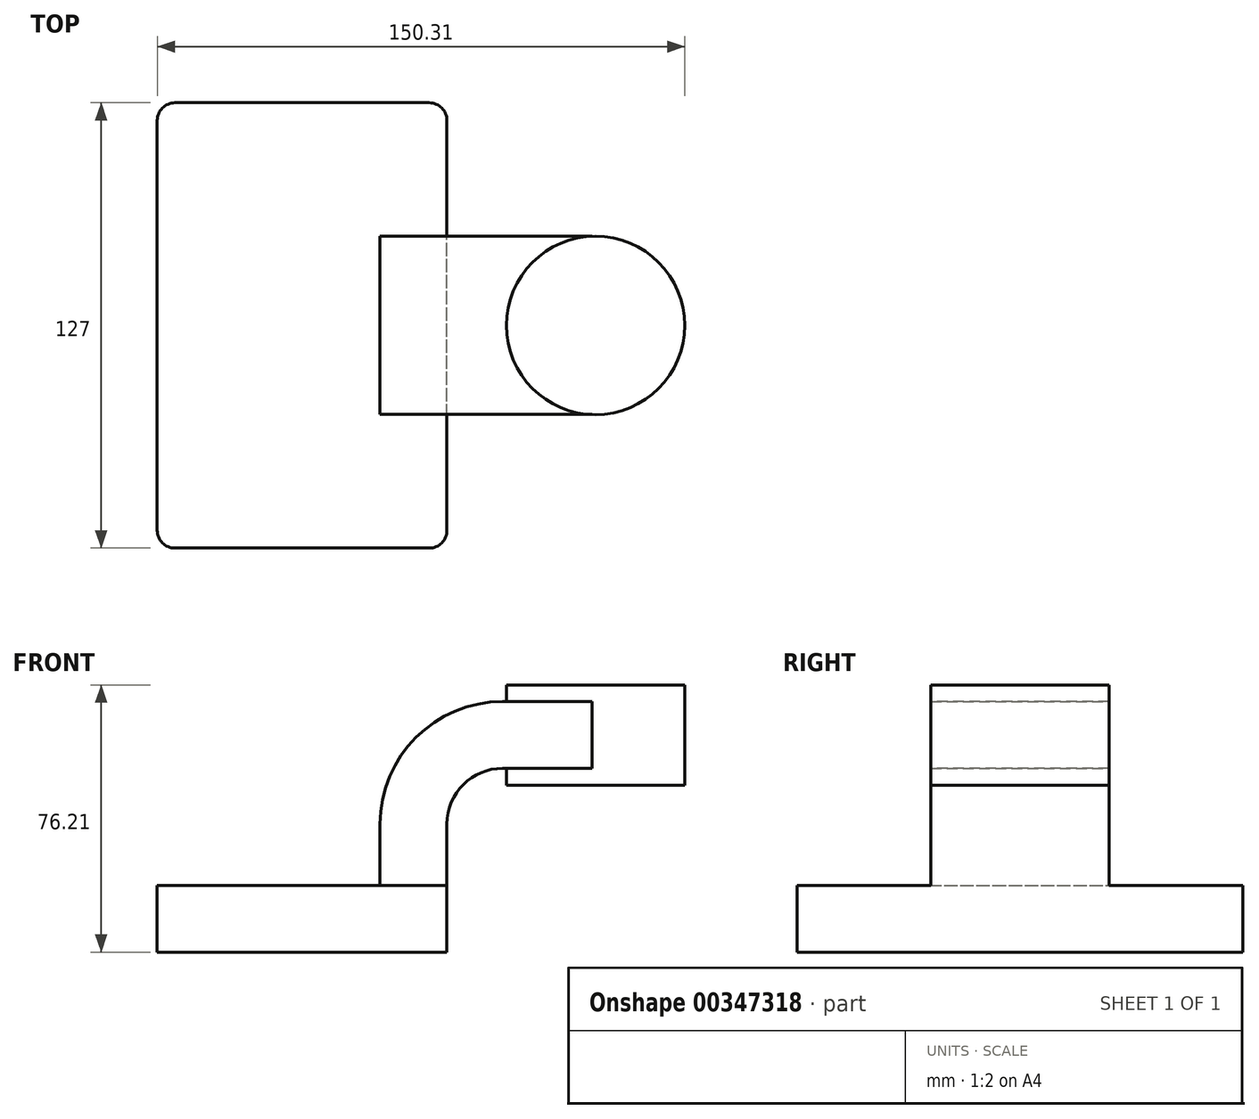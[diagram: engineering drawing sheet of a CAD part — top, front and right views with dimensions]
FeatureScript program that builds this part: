
annotation { "Feature Type Name" : "Feature", "Feature Type Description" : "" }
export const myFeature = defineFeature(function(context is Context, id is Id, definition is map)
    precondition{}
    {
        {
            var Q0;
            Q0=qCreatedBy(makeId("Front.planeOp"),FACE);
            var sketch = newSketch(context, id + "F0", { "sketchPlane" : qUnion([Q0])});
            skLineSegment(sketch, "E0.bottom", {"start": v(41.28, 9.53) * mm, "end": v(-41.28, 9.53) * mm});
            skLineSegment(sketch, "E0.top", {"start": v(41.28, -9.53) * mm, "end": v(-41.28, -9.53) * mm});
            skLineSegment(sketch, "E0.left", {"start": v(41.28, 9.53) * mm, "end": v(41.28, -9.53) * mm});
            skLineSegment(sketch, "E0.right", {"start": v(-41.28, 9.53) * mm, "end": v(-41.28, -9.53) * mm});
            skPoint(sketch, "E0.middle", {"position": v(0, 0) * mm});
            skLineSegment(sketch, "E1.bottom", {"start": v(109.04, 38.1) * mm, "end": v(58.24, 38.1) * mm});
            skLineSegment(sketch, "E1.top", {"start": v(109.04, 66.68) * mm, "end": v(58.24, 66.68) * mm});
            skLineSegment(sketch, "E1.left", {"start": v(109.04, 38.1) * mm, "end": v(109.04, 66.68) * mm});
            skLineSegment(sketch, "E1.right", {"start": v(58.24, 38.1) * mm, "end": v(58.24, 66.68) * mm});
            skPoint(sketch, "E1.middle", {"position": v(83.64, 52.39) * mm});
            skLineSegment(sketch, "E2", {"start": v(41.28, 9.53) * mm, "end": v(41.28, 27) * mm});
            skArc(sketch, "E3", {"start": v(41.27, 27) * mm, "mid": v(45.92, 38.23) * mm, "end": v(57.15, 42.88) * mm});
            skLineSegment(sketch, "E4", {"start": v(57.15, 42.88) * mm, "end": v(83.64, 42.88) * mm});
            skArc(sketch, "E5.0", {"start": v(22.22, 27) * mm, "mid": v(32.45, 51.7) * mm, "end": v(57.15, 61.93) * mm});
            skLineSegment(sketch, "E6.0", {"start": v(22.22, 9.53) * mm, "end": v(22.22, 27) * mm});
            skLineSegment(sketch, "E7.0", {"start": v(57.15, 61.93) * mm, "end": v(83.62, 61.93) * mm});
            skLineSegment(sketch, "E8", {"start": v(83.62, 66.68) * mm, "end": v(83.62, 38.1) * mm});
            skPoint(sketch, "E8.startSnap0", {"position": v(83.64, 66.68) * mm});
            skFitSpline(sketch, "E9", {"points": [v(-41.28, 9.53) * mm, v(57.15, 61.93) * mm], "startDerivative": vector(49, 106.39) * mm, "endDerivative": vector(66.54, -7.38) * mm});
            skSolve(sketch);
        }
        {
            var Q0;
            Q0=makeQuery(id+"F0.imprint","IMPRINT",FACE,{"disambiguationData":[TD([[makeQuery(id+"F0.imprint","IMPRINT",EDGE,{"derivedFrom":sQuery(id+"F0.wireOp",EDGE,"E0.top")}),-1.0]])]});
            extrude(context, id + "F1", {"entities" : qUnion([Q0]), "endBound" : BoundingType.SYMMETRIC, "depth" : 127 * mm});
        }
        {
            var Q0;
            {var subQ0=sQuery(id+"F0.wireOp",EDGE,"E4");var subQ1=sQuery(id+"F0.wireOp",EDGE,"E1.right");var subQ2=makeQuery(id+"F0.imprint","INTERSECT",VERTEX,{"derivedFrom":[subQ1,subQ0]});Q0=makeQuery(id+"F0.imprint","IMPRINT",FACE,{"disambiguationData":[TD([[makeQuery(id+"F0.imprint","IMPRINT",EDGE,{"disambiguationData":[TD([[subQ2,-1.0]])],"derivedFrom":subQ1}),-1.0]])]});}
            var Q1;
            {var subQ1=sQuery(id+"F0.wireOp",EDGE,"E2");Q1=makeQuery(id+"F0.imprint","IMPRINT",FACE,{"disambiguationData":[TD([[makeQuery(id+"F0.imprint","IMPRINT",EDGE,{"derivedFrom":subQ1}),1.0]])]});}
            extrude(context, id + "F2", {"entities" : qUnion([Q0, Q1]), "operationType" : NewBodyOperationType.ADD, "endBound" : BoundingType.SYMMETRIC, "depth" : 50.8 * mm});
        }
        {
            var Q0;
            Q0=makeQuery(id+"F0.imprint","IMPRINT",FACE,{"disambiguationData":[TD([[makeQuery(id+"F0.imprint","IMPRINT",EDGE,{"derivedFrom":sQuery(id+"F0.wireOp",EDGE,"E5.0")}),1.0]])]});
            extrude(context, id + "F3", {"entities" : qUnion([Q0]), "operationType" : NewBodyOperationType.ADD, "endBound" : BoundingType.SYMMETRIC, "depth" : 15.88 * mm});
        }
        {
            var Q0;
            {var subQ4=sQuery(id+"F0.wireOp",EDGE,"E1.left");Q0=makeQuery(id+"F0.imprint","IMPRINT",FACE,{"disambiguationData":[TD([[makeQuery(id+"F0.imprint","IMPRINT",EDGE,{"derivedFrom":subQ4}),1.0]])]});}
            var Q1;
            Q1=sQuery(id+"F0.wireOp",EDGE,"E8");
            revolve(context, id + "F4", {"operationType" : NewBodyOperationType.ADD, "entities" : qUnion([Q0]), "axis" : qUnion([Q1]), "revolveType" : RevolveType.FULL});
        }
        {
            var Q0;
            Q0=makeQuery(id+"F1.opExtrude","CAP_EDGE",EDGE,{"disambiguationData":[OSD([sQuery(id+"F0.wireOp",EDGE,"E0.right")])],"isStart":false});
            var Q1;
            Q1=makeQuery(id+"F1.opExtrude","CAP_EDGE",EDGE,{"disambiguationData":[OSD([sQuery(id+"F0.wireOp",EDGE,"E0.right")])],"isStart":true});
            var Q2;
            Q2=makeQuery(id+"F1.opExtrude","CAP_EDGE",EDGE,{"disambiguationData":[OSD([sQuery(id+"F0.wireOp",EDGE,"E0.left")])],"isStart":true});
            var Q3;
            Q3=makeQuery(id+"F1.opExtrude","CAP_EDGE",EDGE,{"disambiguationData":[OSD([sQuery(id+"F0.wireOp",EDGE,"E0.left")])],"isStart":false});
            fillet(context, id + "F5", {"entities" : qUnion([Q0, Q1, Q2, Q3]), "radius" : 5.08 * mm, "tangentPropagation" : true, "allowEdgeOverflow" : false});
        }
    });
